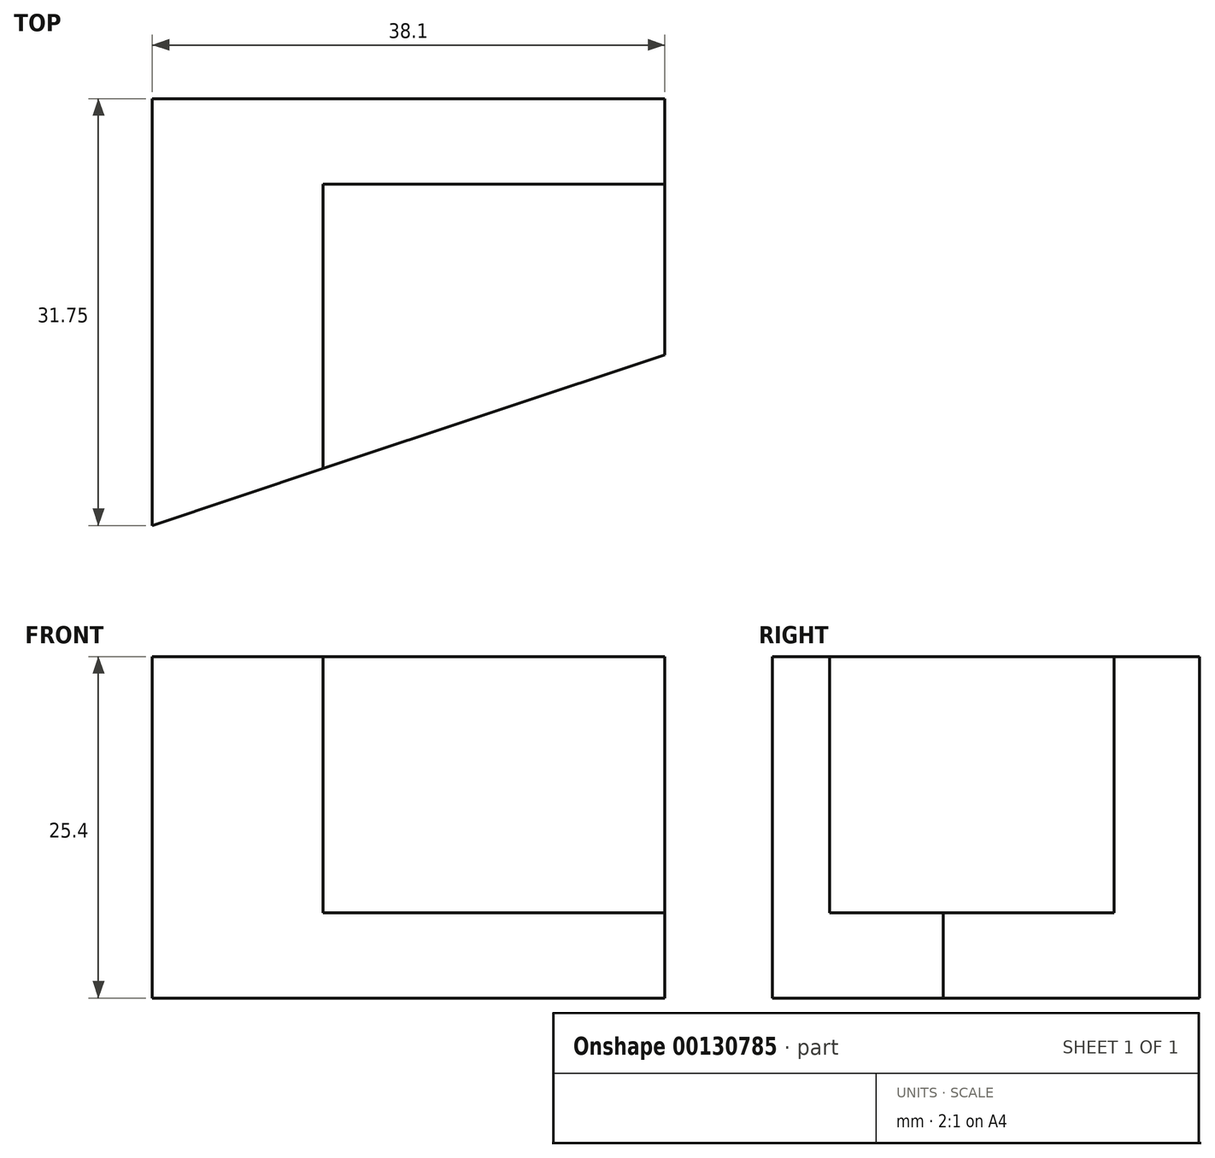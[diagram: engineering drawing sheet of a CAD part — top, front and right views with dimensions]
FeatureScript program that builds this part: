
annotation { "Feature Type Name" : "Feature", "Feature Type Description" : "" }
export const myFeature = defineFeature(function(context is Context, id is Id, definition is map)
    precondition{}
    {
        {
            var Q0;
            Q0=qCreatedBy(makeId("Top.planeOp"),FACE);
            var sketch = newSketch(context, id + "F0", { "sketchPlane" : qUnion([Q0])});
            skLineSegment(sketch, "E0.bottom", {"start": v(0, 0) * mm, "end": v(38.1, 0) * mm});
            skLineSegment(sketch, "E0.top", {"start": v(0, 31.75) * mm, "end": v(38.1, 31.75) * mm});
            skLineSegment(sketch, "E0.left", {"start": v(0, 0) * mm, "end": v(0, 31.75) * mm});
            skLineSegment(sketch, "E0.right", {"start": v(38.1, 0) * mm, "end": v(38.1, 31.75) * mm});
            skSolve(sketch);
        }
        {
            var Q0;
            Q0 = qSketchRegion(id + "F0", true);
            extrude(context, id + "F1", {"entities" : qUnion([Q0]), "depth" : 25.4 * mm});
        }
        {
            var Q0;
            Q0=makeQuery(id+"F1.opExtrude","CAP_FACE",FACE,{"disambiguationData":[OSD([sQuery(id+"F0.wireOp",EDGE,"E0.bottom"),sQuery(id+"F0.wireOp",EDGE,"E0.top"),sQuery(id+"F0.wireOp",EDGE,"E0.left"),sQuery(id+"F0.wireOp",EDGE,"E0.right")])],"isStart":false});
            var sketch = newSketch(context, id + "F2", { "sketchPlane" : qUnion([Q0])});
            skLineSegment(sketch, "E1.bottom", {"start": v(12.7, 25.4) * mm, "end": v(38.1, 25.4) * mm});
            skLineSegment(sketch, "E1.top", {"start": v(12.7, 0) * mm, "end": v(38.1, 0) * mm});
            skLineSegment(sketch, "E1.left", {"start": v(12.7, 25.4) * mm, "end": v(12.7, 0) * mm});
            skLineSegment(sketch, "E1.right", {"start": v(38.1, 25.4) * mm, "end": v(38.1, 0) * mm});
            skSolve(sketch);
        }
        {
            var Q0;
            Q0=makeQuery(id+"F2.imprint","IMPRINT",FACE,{"disambiguationData":[TD([[makeQuery(id+"F2.imprint","IMPRINT",EDGE,{"derivedFrom":sQuery(id+"F2.wireOp",EDGE,"E1.bottom")}),-1.0]])]});
            extrude(context, id + "F3", {"entities" : qUnion([Q0]), "operationType" : NewBodyOperationType.REMOVE, "oppositeDirection" : true, "depth" : 19.05 * mm});
        }
        {
            var Q0;
            Q0=qCreatedBy(makeId("Top.planeOp"),FACE);
            var sketch = newSketch(context, id + "F4", { "sketchPlane" : qUnion([Q0])});
            skLineSegment(sketch, "E2", {"start": v(0, 0) * mm, "end": v(38.1, 12.7) * mm});
            skLineSegment(sketch, "E3", {"start": v(0, 0) * mm, "end": v(38.1, 0) * mm});
            skLineSegment(sketch, "E4", {"start": v(38.1, 0) * mm, "end": v(38.1, 12.7) * mm});
            skSolve(sketch);
        }
        {
            var Q0;
            Q0=makeQuery(id+"F4.imprint","IMPRINT",FACE,{"disambiguationData":[TD([[makeQuery(id+"F4.imprint","IMPRINT",EDGE,{"derivedFrom":sQuery(id+"F4.wireOp",EDGE,"E2")}),-1.0]])]});
            extrude(context, id + "F5", {"entities" : qUnion([Q0]), "operationType" : NewBodyOperationType.REMOVE, "depth" : 25.4 * mm});
        }
    });
